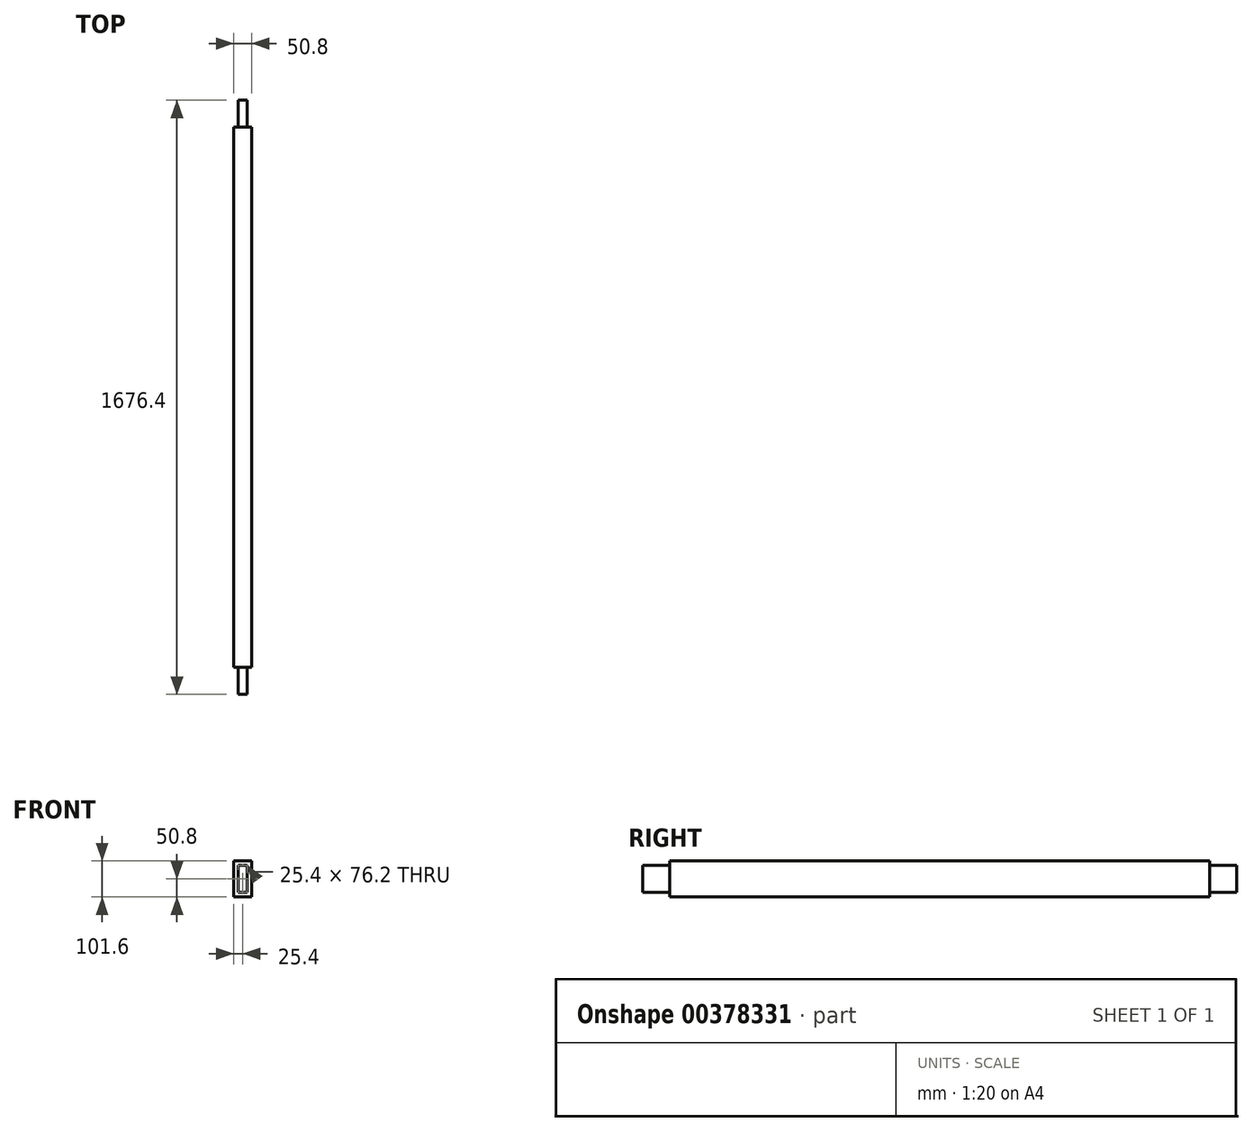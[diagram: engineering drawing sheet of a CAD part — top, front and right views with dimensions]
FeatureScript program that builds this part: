
annotation { "Feature Type Name" : "Feature", "Feature Type Description" : "" }
export const myFeature = defineFeature(function(context is Context, id is Id, definition is map)
    precondition{}
    {
        {
            var Q0;
            Q0=qCreatedBy(makeId("Right.planeOp"),FACE);
            var sketch = newSketch(context, id + "F0", { "sketchPlane" : qUnion([Q0])});
            skLineSegment(sketch, "E0.bottom", {"start": v(-762, 50.8) * mm, "end": v(762, 50.8) * mm});
            skLineSegment(sketch, "E0.top", {"start": v(-762, -50.8) * mm, "end": v(762, -50.8) * mm});
            skLineSegment(sketch, "E0.left", {"start": v(-762, 50.8) * mm, "end": v(-762, -50.8) * mm});
            skLineSegment(sketch, "E0.right", {"start": v(762, 50.8) * mm, "end": v(762, -50.8) * mm});
            skSolve(sketch);
        }
        {
            var Q0;
            Q0=makeQuery(id+"F0.imprint","IMPRINT",FACE,{"disambiguationData":[TD([[makeQuery(id+"F0.imprint","IMPRINT",EDGE,{"derivedFrom":sQuery(id+"F0.wireOp",EDGE,"E0.bottom")}),-1.0]])]});
            extrude(context, id + "F1", {"entities" : qUnion([Q0]), "depth" : 25.4 * mm, "hasSecondDirection" : true, "secondDirectionOppositeDirection" : true, "secondDirectionDepth" : 25.4 * mm});
        }
        {
            var Q0;
            Q0=makeQuery(id+"F1.opExtrude","SWEPT_FACE",FACE,{"disambiguationData":[OSD([sQuery(id+"F0.wireOp",EDGE,"E0.right")])]});
            var sketch = newSketch(context, id + "F2", { "sketchPlane" : qUnion([Q0])});
            skLineSegment(sketch, "E1.bottom", {"start": v(-12.7, 38.1) * mm, "end": v(12.7, 38.1) * mm});
            skLineSegment(sketch, "E1.top", {"start": v(-12.7, -38.1) * mm, "end": v(12.7, -38.1) * mm});
            skLineSegment(sketch, "E1.left", {"start": v(-12.7, 38.1) * mm, "end": v(-12.7, -38.1) * mm});
            skLineSegment(sketch, "E1.right", {"start": v(12.7, 38.1) * mm, "end": v(12.7, -38.1) * mm});
            skSolve(sketch);
        }
        {
            var Q0;
            Q0=makeQuery(id+"F2.imprint","IMPRINT",FACE,{"disambiguationData":[TD([[makeQuery(id+"F2.imprint","IMPRINT",EDGE,{"derivedFrom":sQuery(id+"F2.wireOp",EDGE,"E1.bottom")}),-1.0]])]});
            extrude(context, id + "F3", {"entities" : qUnion([Q0]), "operationType" : NewBodyOperationType.ADD, "depth" : 76.2 * mm});
        }
        {
            var Q0;
            Q0=makeQuery(id+"F1.opExtrude","SWEPT_FACE",FACE,{"disambiguationData":[OSD([sQuery(id+"F0.wireOp",EDGE,"E0.left")])]});
            var sketch = newSketch(context, id + "F4", { "sketchPlane" : qUnion([Q0])});
            skLineSegment(sketch, "E2.bottom", {"start": v(-12.7, 38.1) * mm, "end": v(12.7, 38.1) * mm});
            skLineSegment(sketch, "E2.top", {"start": v(-12.7, -38.1) * mm, "end": v(12.7, -38.1) * mm});
            skLineSegment(sketch, "E2.left", {"start": v(-12.7, 38.1) * mm, "end": v(-12.7, -38.1) * mm});
            skLineSegment(sketch, "E2.right", {"start": v(12.7, 38.1) * mm, "end": v(12.7, -38.1) * mm});
            skSolve(sketch);
        }
        {
            var Q0;
            Q0=makeQuery(id+"F4.imprint","IMPRINT",FACE,{"disambiguationData":[TD([[makeQuery(id+"F4.imprint","IMPRINT",EDGE,{"derivedFrom":sQuery(id+"F4.wireOp",EDGE,"E2.bottom")}),-1.0]])]});
            extrude(context, id + "F5", {"entities" : qUnion([Q0]), "operationType" : NewBodyOperationType.ADD, "depth" : 76.2 * mm});
        }
    });
